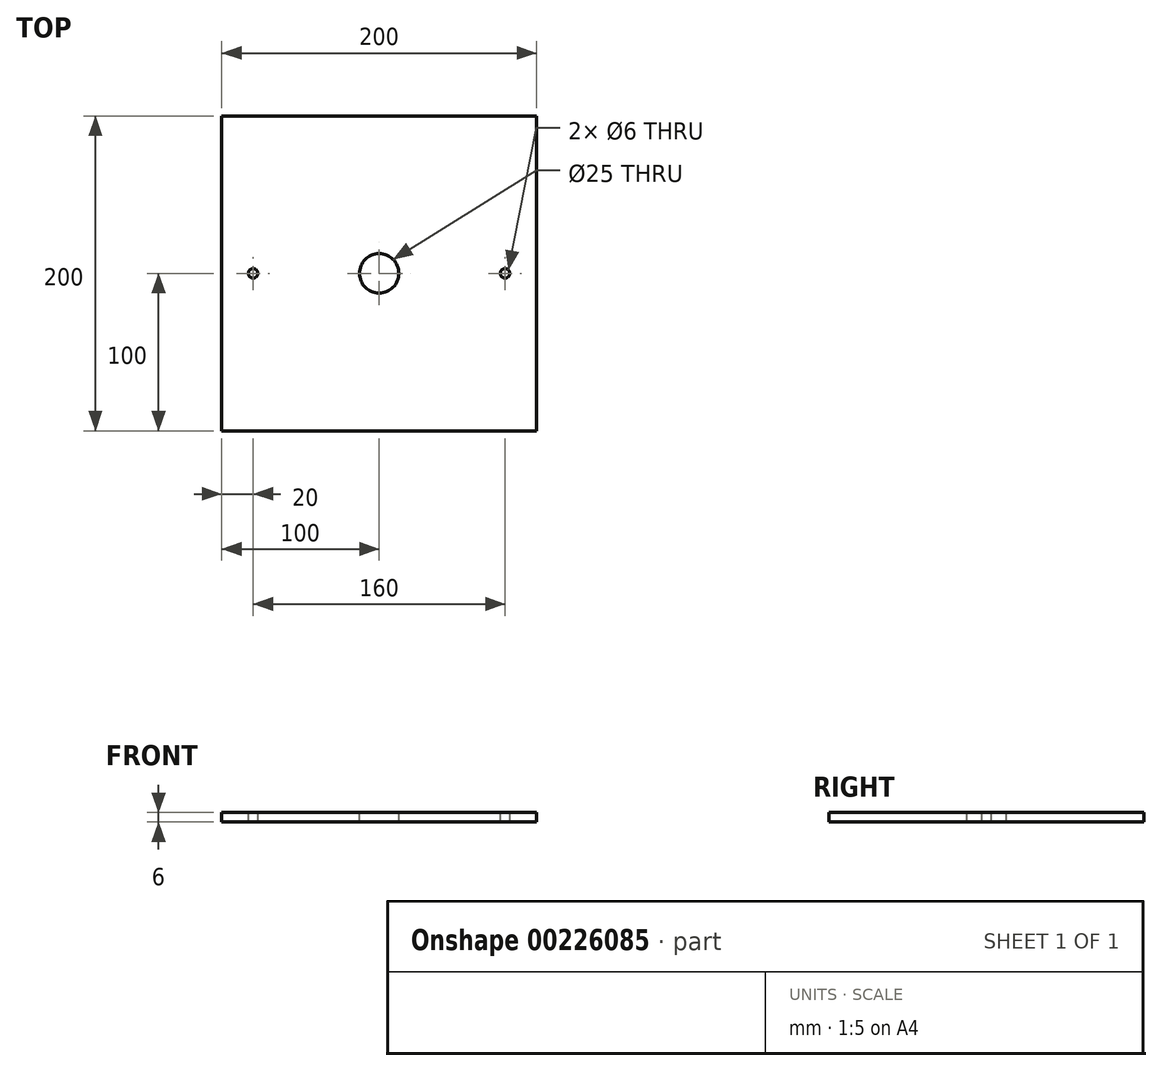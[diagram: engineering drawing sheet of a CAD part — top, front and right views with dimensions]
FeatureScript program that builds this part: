
annotation { "Feature Type Name" : "Feature", "Feature Type Description" : "" }
export const myFeature = defineFeature(function(context is Context, id is Id, definition is map)
    precondition{}
    {
        {
            var Q0;
            Q0=qCreatedBy(makeId("Top.planeOp"),FACE);
            var sketch = newSketch(context, id + "F0", { "sketchPlane" : qUnion([Q0])});
            skLineSegment(sketch, "E0.bottom", {"start": v(0, 0) * mm, "end": v(200, 0) * mm});
            skLineSegment(sketch, "E0.top", {"start": v(0, 200) * mm, "end": v(200, 200) * mm});
            skLineSegment(sketch, "E0.left", {"start": v(0, 0) * mm, "end": v(0, 200) * mm});
            skLineSegment(sketch, "E0.right", {"start": v(200, 0) * mm, "end": v(200, 200) * mm});
            skSolve(sketch);
        }
        {
            var Q0;
            Q0=makeQuery(id+"F0.imprint","IMPRINT",FACE,{"disambiguationData":[TD([[makeQuery(id+"F0.imprint","IMPRINT",EDGE,{"derivedFrom":sQuery(id+"F0.wireOp",EDGE,"E0.bottom")}),1.0]])]});
            extrude(context, id + "F1", {"entities" : qUnion([Q0]), "depth" : 6 * mm});
        }
        {
            var Q0;
            Q0=makeQuery(id+"F1.opExtrude","CAP_FACE",FACE,{"disambiguationData":[OSD([sQuery(id+"F0.wireOp",EDGE,"E0.bottom"),sQuery(id+"F0.wireOp",EDGE,"E0.top"),sQuery(id+"F0.wireOp",EDGE,"E0.left"),sQuery(id+"F0.wireOp",EDGE,"E0.right")])],"isStart":false});
            var sketch = newSketch(context, id + "F2", { "sketchPlane" : qUnion([Q0])});
            skLineSegment(sketch, "E1", {"start": v(0, 100) * mm, "end": v(200, 100) * mm, "construction": true});
            skCircle(sketch, "E2", {"center": v(20, 100) * mm, "radius": 3 * mm});
            skLineSegment(sketch, "E3", {"start": v(100, 100) * mm, "end": v(100, 139.05) * mm, "construction": true});
            skCircle(sketch, "E4.MirrorC", {"center": v(180, 100) * mm, "radius": 3 * mm});
            skSolve(sketch);
        }
        {
            var Q0;
            Q0=sQuery(id+"F2.wireOp",VERTEX,"E2.center");
            var Q1;
            Q1=sQuery(id+"F2.wireOp",VERTEX,"E4.MirrorC.center");
            var Q2;
            Q2=makeQuery(id+"F1.opExtrude","SWEPT_BODY",BODY,{"disambiguationData":[OSD([sQuery(id+"F0.wireOp",EDGE,"E0.bottom"),sQuery(id+"F0.wireOp",EDGE,"E0.top"),sQuery(id+"F0.wireOp",EDGE,"E0.left"),sQuery(id+"F0.wireOp",EDGE,"E0.right")])]});
            hole(context, id + "F3", {"style" : HoleStyle.SIMPLE, "endStyle" : HoleEndStyle.THROUGH, "holeDiameter" : 6 * mm, "locations" : qUnion([Q0, Q1]), "scope" : qUnion([Q2]), "isTappedThrough" : true});
        }
        {
            var Q0;
            Q0=makeQuery(id+"F1.opExtrude","CAP_FACE",FACE,{"disambiguationData":[OSD([sQuery(id+"F0.wireOp",EDGE,"E0.bottom"),sQuery(id+"F0.wireOp",EDGE,"E0.top"),sQuery(id+"F0.wireOp",EDGE,"E0.left"),sQuery(id+"F0.wireOp",EDGE,"E0.right")])],"isStart":false});
            var sketch = newSketch(context, id + "F4", { "sketchPlane" : qUnion([Q0])});
            skLineSegment(sketch, "E5", {"start": v(0, 100) * mm, "end": v(200, 100) * mm, "construction": true});
            skLineSegment(sketch, "E6", {"start": v(100, 100) * mm, "end": v(100, 147.2) * mm, "construction": true});
            skCircle(sketch, "E7", {"center": v(100, 100) * mm, "radius": 12.5 * mm});
            skSolve(sketch);
        }
        {
            var Q0;
            Q0=sQuery(id+"F4.wireOp",VERTEX,"E7.center");
            var Q1;
            Q1=makeQuery(id+"F1.opExtrude","SWEPT_BODY",BODY,{"disambiguationData":[OSD([sQuery(id+"F0.wireOp",EDGE,"E0.bottom"),sQuery(id+"F0.wireOp",EDGE,"E0.top"),sQuery(id+"F0.wireOp",EDGE,"E0.left"),sQuery(id+"F0.wireOp",EDGE,"E0.right")])]});
            hole(context, id + "F5", {"style" : HoleStyle.SIMPLE, "endStyle" : HoleEndStyle.THROUGH, "holeDiameter" : 25 * mm, "locations" : qUnion([Q0]), "scope" : qUnion([Q1]), "isTappedThrough" : true});
        }
    });
